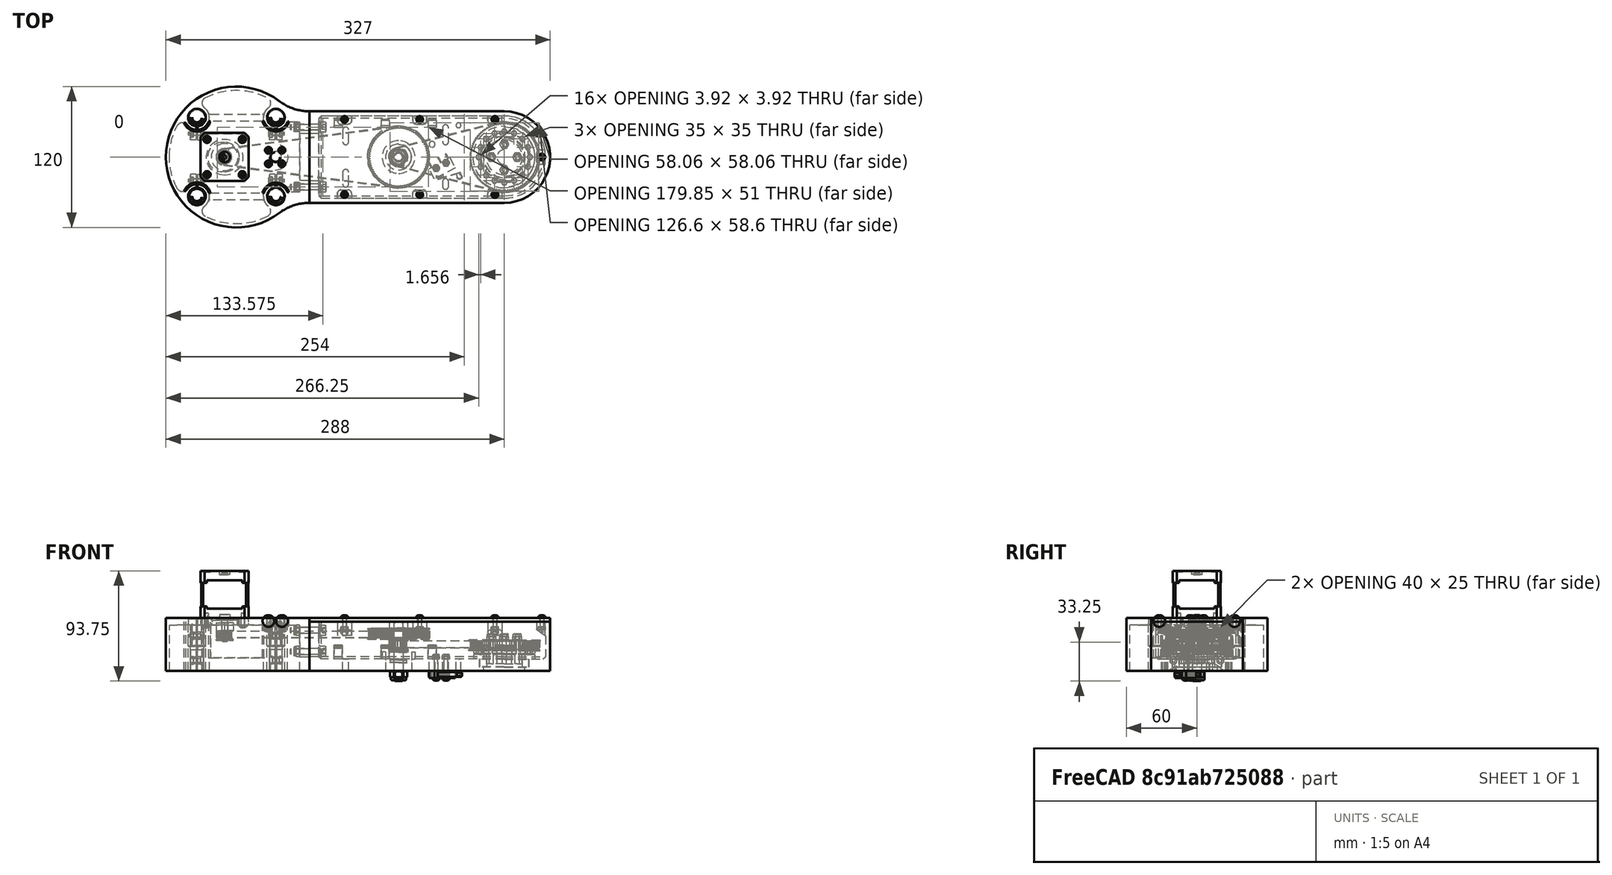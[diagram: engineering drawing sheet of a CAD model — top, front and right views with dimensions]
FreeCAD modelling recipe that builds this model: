
FCSTD DOCUMENT  (FreeCAD 0.19R)
Label: Arm1_a2p
License: All rights reserved
LicenseURL: http://en.wikipedia.org/wiki/All_rights_reserved
objects: Part::FeaturePython×76, App::FeaturePython×51, Spreadsheet::Sheet×2
note: 76 computed .brp shape members not serialized (recipe doc carries the construction recipe); baked Part::Feature solids carry a one-line shape summary decoded from their .brp

FEATURE [Part::FeaturePython] b_Arm1_modified_001_  label="Arm1_modified_001"  # a2plus imported part (geometry in sourceFile) (typed FeaturePython)
  a2p_Version = V0.1
  fixedPosition = true
  muxInfo = <blob: 26988 chars omitted>
  objectType = a2pPart
  sourceFile = ./Arm1_modified.FCStd
  subassemblyImport = false
  timeLastImport = 1.62074e+09
  updateColors = true
FEATURE [App::FeaturePython] circularEdge_001_mirror  label="circularEdge_001__Z-axis_mount_platform_LM8_001"  # a2plus constraint (typed FeaturePython)
  Object1 = b_Z_axis_mount_platform_LM8_001_
  Object2 = b_Arm1_modified_001_
  ParentTreeObject = -> b_Arm1_modified_001_
  SubElement1 = Edge12
  SubElement2 = Edge175
  Suppressed = false
  Type = circularEdge
  directionConstraint = 1
  lockRotation = true
  offset = 0
FEATURE [Part::FeaturePython] b_Ball_bearing_6081_001_  label="Ball_bearing_6081_001"  # a2plus imported part (geometry in sourceFile) (typed FeaturePython)
  Placement = pos=(-90,-3.743e-12,9) rot=(1,0,0;1.5708rad)
  a2p_Version = V0.1
  fixedPosition = false
  muxInfo = <blob: 2406 chars omitted>
  objectType = a2pPart
  sourceFile = ./Ball_bearing_608.step
  subassemblyImport = false
  timeLastImport = 1.62025e+09
  updateColors = true
FEATURE [App::FeaturePython] circularEdge_002  label="circularEdge_002__Arm1_modified_001"  # a2plus constraint (typed FeaturePython)
  Object1 = b_Ball_bearing_6081_001_
  Object2 = b_Arm1_modified_001_
  ParentTreeObject = -> b_Ball_bearing_6081_001_
  SubElement1 = Edge43
  SubElement2 = Edge634
  Suppressed = false
  Type = circularEdge
  directionConstraint = 1
  lockRotation = false
  offset = 0
FEATURE [App::FeaturePython] circularEdge_002_mirror  label="circularEdge_002__Ball_bearing_6081_001"  # a2plus constraint (typed FeaturePython)
  Object1 = b_Ball_bearing_6081_001_
  Object2 = b_Arm1_modified_001_
  ParentTreeObject = -> b_Arm1_modified_001_
  SubElement1 = Edge43
  SubElement2 = Edge634
  Suppressed = false
  Type = circularEdge
  directionConstraint = 1
  lockRotation = false
  offset = 0
FEATURE [Part::FeaturePython] b_Ball_bearing_6081_001_001  label="Ball_bearing_6081_002"  # a2plus imported part (geometry in sourceFile) (typed FeaturePython)
  Placement = pos=(-90,-1.2387e-07,-8.87936e-09) rot=(1,0,0;1.5708rad)
  a2p_Version = V0.1
  fixedPosition = false
  muxInfo = <blob: 2406 chars omitted>
  objectType = a2pPart
  sourceFile = ./Ball_bearing_608.step
  subassemblyImport = false
  timeLastImport = 1.62025e+09
  updateColors = true
FEATURE [App::FeaturePython] circularEdge_003  label="circularEdge_003__Arm1_modified_001"  # a2plus constraint (typed FeaturePython)
  Object1 = b_Ball_bearing_6081_001_001
  Object2 = b_Arm1_modified_001_
  ParentTreeObject = -> b_Ball_bearing_6081_001_001
  SubElement1 = Edge13
  SubElement2 = Edge459
  Suppressed = false
  Type = circularEdge
  directionConstraint = 1
  lockRotation = false
  offset = 0
FEATURE [App::FeaturePython] circularEdge_003_mirror  label="circularEdge_003__Ball_bearing_6081_002"  # a2plus constraint (typed FeaturePython)
  Object1 = b_Ball_bearing_6081_001_001
  Object2 = b_Arm1_modified_001_
  ParentTreeObject = -> b_Arm1_modified_001_
  SubElement1 = Edge13
  SubElement2 = Edge459
  Suppressed = false
  Type = circularEdge
  directionConstraint = 1
  lockRotation = false
  offset = 0
FEATURE [Part::FeaturePython] b_Ball_bearing_68061_001_  label="Ball_bearing_68061_001"  # a2plus imported part (geometry in sourceFile) (typed FeaturePython)
  Placement = pos=(0,1e-15,3) rot=(1,0,0;1.5708rad)
  a2p_Version = V0.1
  fixedPosition = false
  muxInfo = <blob: 2407 chars omitted>
  objectType = a2pPart
  sourceFile = ./Ball_bearing_6806.step
  subassemblyImport = false
  timeLastImport = 1.62074e+09
  updateColors = true
FEATURE [App::FeaturePython] circularEdge_004  label="circularEdge_004__Arm1_modified_001"  # a2plus constraint (typed FeaturePython)
  Object1 = b_Ball_bearing_68061_001_
  Object2 = b_Arm1_modified_001_
  ParentTreeObject = -> b_Ball_bearing_68061_001_
  SubElement1 = Edge21
  SubElement2 = Edge539
  Suppressed = false
  Type = circularEdge
  directionConstraint = 1
  lockRotation = false
  offset = 0
FEATURE [App::FeaturePython] circularEdge_004_mirror  label="circularEdge_004__Ball_bearing_68061_001"  # a2plus constraint (typed FeaturePython)
  Object1 = b_Ball_bearing_68061_001_
  Object2 = b_Arm1_modified_001_
  ParentTreeObject = -> b_Arm1_modified_001_
  SubElement1 = Edge21
  SubElement2 = Edge539
  Suppressed = false
  Type = circularEdge
  directionConstraint = 1
  lockRotation = false
  offset = 0
FEATURE [Part::FeaturePython] b_Thrust_bearing_511071_001_  label="Thrust_bearing_511071_001"  # a2plus imported part (geometry in sourceFile) (typed FeaturePython)
  Placement = pos=(0,2e-15,10) rot=(1,0,0;1.5708rad)
  a2p_Version = V0.1
  fixedPosition = false
  muxInfo = <blob: 16793 chars omitted>
  objectType = a2pPart
  sourceFile = ./Thrust_bearing_51107.step
  subassemblyImport = false
  timeLastImport = 1.62025e+09
  updateColors = true
FEATURE [App::FeaturePython] circularEdge_005  label="circularEdge_005__Arm1_modified_001"  # a2plus constraint (typed FeaturePython)
  Object1 = b_Thrust_bearing_511071_001_
  Object2 = b_Arm1_modified_001_
  ParentTreeObject = -> b_Thrust_bearing_511071_001_
  SubElement1 = Edge18
  SubElement2 = Edge395
  Suppressed = false
  Type = circularEdge
  directionConstraint = 1
  lockRotation = false
  offset = 0
FEATURE [App::FeaturePython] circularEdge_005_mirror  label="circularEdge_005__Thrust_bearing_511071_001"  # a2plus constraint (typed FeaturePython)
  Object1 = b_Thrust_bearing_511071_001_
  Object2 = b_Arm1_modified_001_
  ParentTreeObject = -> b_Arm1_modified_001_
  SubElement1 = Edge18
  SubElement2 = Edge395
  Suppressed = false
  Type = circularEdge
  directionConstraint = 1
  lockRotation = false
  offset = 0
FEATURE [Part::FeaturePython] b_Pulley_GT2_92t_j21_001_  label="Pulley_GT2-92t_j21_001"  # a2plus imported part (geometry in sourceFile) (typed FeaturePython)
  Placement = pos=(0,8.12133e-08,18.2) rot=(1,0,0;1.5708rad)
  a2p_Version = V0.1
  fixedPosition = false
  muxInfo = <blob: 117975 chars omitted>
  objectType = a2pPart
  sourceFile = ./Pulley_GT2-92t_j2.step
  subassemblyImport = false
  timeLastImport = 1.62074e+09
  updateColors = true
FEATURE [App::FeaturePython] circularEdge_006  label="circularEdge_006__Thrust_bearing_511071_001"  # a2plus constraint (typed FeaturePython)
  Object1 = b_Pulley_GT2_92t_j21_001_
  Object2 = b_Thrust_bearing_511071_001_
  ParentTreeObject = -> b_Pulley_GT2_92t_j21_001_
  SubElement1 = Edge2523
  SubElement2 = Edge29
  Suppressed = false
  Type = circularEdge
  directionConstraint = 1
  lockRotation = false
  offset = 0
FEATURE [App::FeaturePython] circularEdge_006_mirror  label="circularEdge_006__Pulley_GT2-92t_j21_001"  # a2plus constraint (typed FeaturePython)
  Object1 = b_Pulley_GT2_92t_j21_001_
  Object2 = b_Thrust_bearing_511071_001_
  ParentTreeObject = -> b_Thrust_bearing_511071_001_
  SubElement1 = Edge2523
  SubElement2 = Edge29
  Suppressed = false
  Type = circularEdge
  directionConstraint = 1
  lockRotation = false
  offset = 0
FEATURE [Part::FeaturePython] Washer  label="M8-Washer"  # Fasteners workbench fastener (typed FeaturePython)
  Placement = pos=(-90,1.17671e-07,16) rot=(0,0,1;0rad)
  baseObject = -> b_Ball_bearing_6081_001_ [Edge39]
  diameter = 8
  invert = true
  matchOuter = false
  offset = 0
  type = 3
FEATURE [Part::FeaturePython] b_Pulley_GT2_23t_80t_arm11_001_  label="Pulley_GT2-23t_80t_arm11_001"  # a2plus imported part (geometry in sourceFile) (typed FeaturePython)
  Placement = pos=(-90,9.54168e-07,35.05) rot=(0.229954,-0.688157,0.688157;3.59364rad)
  a2p_Version = V0.1
  fixedPosition = false
  muxInfo = <blob: 130900 chars omitted>
  objectType = a2pPart
  sourceFile = ./Pulley_GT2-23t_80t_arm1.step
  subassemblyImport = false
  timeLastImport = 1.62074e+09
  updateColors = true
FEATURE [App::FeaturePython] circularEdge_007  label="circularEdge_007__Ball_bearing_6081_001"  # a2plus constraint (typed FeaturePython)
  Object1 = b_Pulley_GT2_23t_80t_arm11_001_
  Object2 = b_Ball_bearing_6081_001_
  ParentTreeObject = -> b_Pulley_GT2_23t_80t_arm11_001_
  SubElement1 = Edge2268
  SubElement2 = Edge13
  Suppressed = false
  Type = circularEdge
  directionConstraint = 1
  lockRotation = false
  offset = -1.45
FEATURE [App::FeaturePython] circularEdge_007_mirror  label="circularEdge_007__Pulley_GT2-23t_80t_arm11_001"  # a2plus constraint (typed FeaturePython)
  Object1 = b_Pulley_GT2_23t_80t_arm11_001_
  Object2 = b_Ball_bearing_6081_001_
  ParentTreeObject = -> b_Ball_bearing_6081_001_
  SubElement1 = Edge2268
  SubElement2 = Edge13
  Suppressed = false
  Type = circularEdge
  directionConstraint = 1
  lockRotation = false
  offset = -1.45
FEATURE [Part::FeaturePython] b_Belt_GT2_300mm_23_92_arm11_001_  label="Belt_GT2_300mm_23-92_arm11_001"  # a2plus imported part (geometry in sourceFile) (typed FeaturePython)
  Placement = pos=(-2.93982e-09,1.75969e-07,19.65) rot=(1,0,0;1.5708rad)
  a2p_Version = V0.1
  fixedPosition = false
  muxInfo = [VERTEXES] | V;Part__Feature;1; | V;Part__Feature;2; | V;Part__Feature;3; | V;Part__Feature;4; | V;Part__Feature;5; | V;Part__Feature;6; | V;Part__Feature;7; | V;Part__Feature;8; | V;Part__Feature;9; | V;Part__Feature;10; | V;Part__Feature;11; | V;Part__Feature;12; | V;Part__Feature;13; | V;Part__Feature;14; | V;Part__Feature;15; | V;Part__Feature;16; | V;Part__Feature;17; | V;Part__Feature;18; | V;Part__Feature;19; | V;Part__Feature;20; | V;Part__Feature;21; | V;Part__Feature;22; | V;Part__Feature;23; | V;Part__Feature;24; | [EDGES] | E;Part__Feature;1; | E;Part__Feature;2; | E;Part__Feature;3; | E;Part__Feature;4; | E;Part__Feature;2; | E;Part__Feature;5; | E;Part__Feature;4; | E;Part__Feature;6; | E;Part__Feature;7; | E;Part__Feature;8; | E;Part__Feature;9; | E;Part__Feature;6; | E;Part__Feature;8; | E;Part__Feature;10; | E;Part__Feature;11; | E;Part__Feature;12; | E;Part__Feature;6; | E;Part__Feature;13; | E;Part__Feature;14; | E;Part__Feature;15; | E;Part__Feature;16; | E;Part__Feature;4; | E;Part__Feature;17; | E;Part__Feature;18; | E;Part__Feature;8; | E;Part__Feature;19; | E;Part__Feature;20; | E;Part__Feature;21; | E;Part__Feature;2; | E;Part__Feature;22; | E;Part__Feature;23; | E;Part__Feature;24; | E;Part__Feature;25; | E;Part__Feature;26; | E;Part__Feature;27; | E;Part__Feature;28; | [FACES] | F;Part__Feature;1; | F;Part__Feature;1; | F;Part__Feature;2; | F;Part__Feature;2; | F;Part__Feature;3; | F;Part__Feature;4; | F;Part__Feature;5; | F;Part__Feature;6; | F;Part__Feature;2; | F;Part__Feature;7; | F;Part__Feature;8; | F;Part__Feature;9; | F;Part__Feature;1; | F;Part__Feature;10;
  objectType = a2pPart
  sourceFile = ./Belt_GT2_300mm_23-92_arm1.step
  subassemblyImport = false
  timeLastImport = 1.62074e+09
  updateColors = true
FEATURE [App::FeaturePython] circularEdge_001  label="circularEdge_001__Pulley_GT2-23t_80t_arm11_001"  # a2plus constraint (typed FeaturePython)
  Object1 = b_Belt_GT2_300mm_23_92_arm11_001_
  Object2 = b_Pulley_GT2_23t_80t_arm11_001_
  ParentTreeObject = -> b_Belt_GT2_300mm_23_92_arm11_001_
  SubElement1 = Edge15
  SubElement2 = Edge1
  Suppressed = false
  Type = circularEdge
  directionConstraint = 1
  lockRotation = false
  offset = 0
FEATURE [App::FeaturePython] circularEdge_001_mirror001  label="circularEdge_001__Belt_GT2_300mm_23-92_arm11_001"  # a2plus constraint (typed FeaturePython)
  Object1 = b_Belt_GT2_300mm_23_92_arm11_001_
  Object2 = b_Pulley_GT2_23t_80t_arm11_001_
  ParentTreeObject = -> b_Pulley_GT2_23t_80t_arm11_001_
  SubElement1 = Edge15
  SubElement2 = Edge1
  Suppressed = false
  Type = circularEdge
  directionConstraint = 1
  lockRotation = false
  offset = 0
FEATURE [App::FeaturePython] axisCoincident_001  label="axisCoincident_001__Pulley_GT2-92t_j21_001"  # a2plus constraint (typed FeaturePython)
  Object1 = b_Belt_GT2_300mm_23_92_arm11_001_
  Object2 = b_Pulley_GT2_92t_j21_001_
  ParentTreeObject = -> b_Belt_GT2_300mm_23_92_arm11_001_
  SubElement1 = Face3
  SubElement2 = Face12
  Suppressed = false
  Type = axial
  directionConstraint = 0
  lockRotation = false
FEATURE [App::FeaturePython] axisCoincident_001_mirror  label="axisCoincident_001__Belt_GT2_300mm_23-92_arm11_001"  # a2plus constraint (typed FeaturePython)
  Object1 = b_Belt_GT2_300mm_23_92_arm11_001_
  Object2 = b_Pulley_GT2_92t_j21_001_
  ParentTreeObject = -> b_Pulley_GT2_92t_j21_001_
  SubElement1 = Face3
  SubElement2 = Face12
  Suppressed = false
  Type = axial
  directionConstraint = 0
  lockRotation = false
FEATURE [Part::FeaturePython] b_Belt_GT2_400mm_20_80_arm11_001_  label="Belt_GT2_400mm_20-80_arm11_001"  # a2plus imported part (geometry in sourceFile) (typed FeaturePython)
  Placement = pos=(-90,5.96931e-07,28.05) rot=(1,0,0;1.5708rad)
  a2p_Version = V0.1
  fixedPosition = false
  muxInfo = [VERTEXES] | V;Part__Feature;1; | V;Part__Feature;2; | V;Part__Feature;3; | V;Part__Feature;4; | V;Part__Feature;5; | V;Part__Feature;6; | V;Part__Feature;7; | V;Part__Feature;8; | V;Part__Feature;9; | V;Part__Feature;10; | V;Part__Feature;11; | V;Part__Feature;12; | V;Part__Feature;13; | V;Part__Feature;14; | V;Part__Feature;15; | V;Part__Feature;16; | V;Part__Feature;17; | V;Part__Feature;18; | V;Part__Feature;19; | V;Part__Feature;20; | V;Part__Feature;21; | V;Part__Feature;22; | V;Part__Feature;23; | V;Part__Feature;24; | [EDGES] | E;Part__Feature;1; | E;Part__Feature;2; | E;Part__Feature;3; | E;Part__Feature;4; | E;Part__Feature;2; | E;Part__Feature;5; | E;Part__Feature;4; | E;Part__Feature;6; | E;Part__Feature;7; | E;Part__Feature;8; | E;Part__Feature;9; | E;Part__Feature;6; | E;Part__Feature;8; | E;Part__Feature;10; | E;Part__Feature;11; | E;Part__Feature;12; | E;Part__Feature;6; | E;Part__Feature;13; | E;Part__Feature;14; | E;Part__Feature;15; | E;Part__Feature;16; | E;Part__Feature;4; | E;Part__Feature;17; | E;Part__Feature;18; | E;Part__Feature;8; | E;Part__Feature;19; | E;Part__Feature;20; | E;Part__Feature;21; | E;Part__Feature;2; | E;Part__Feature;22; | E;Part__Feature;23; | E;Part__Feature;24; | E;Part__Feature;25; | E;Part__Feature;26; | E;Part__Feature;27; | E;Part__Feature;28; | [FACES] | F;Part__Feature;1; | F;Part__Feature;1; | F;Part__Feature;2; | F;Part__Feature;2; | F;Part__Feature;3; | F;Part__Feature;4; | F;Part__Feature;5; | F;Part__Feature;6; | F;Part__Feature;2; | F;Part__Feature;7; | F;Part__Feature;8; | F;Part__Feature;9; | F;Part__Feature;1; | F;Part__Feature;10;
  objectType = a2pPart
  sourceFile = ./Belt_GT2_400mm_20-80_arm1.step
  subassemblyImport = false
  timeLastImport = 1.62074e+09
  updateColors = true
FEATURE [App::FeaturePython] circularEdge_008  label="circularEdge_008__Pulley_GT2-23t_80t_arm11_001"  # a2plus constraint (typed FeaturePython)
  Object1 = b_Belt_GT2_400mm_20_80_arm11_001_
  Object2 = b_Pulley_GT2_23t_80t_arm11_001_
  ParentTreeObject = -> b_Belt_GT2_400mm_20_80_arm11_001_
  SubElement1 = Edge5
  SubElement2 = Edge107
  Suppressed = false
  Type = circularEdge
  directionConstraint = 0
  lockRotation = false
  offset = 0
FEATURE [App::FeaturePython] circularEdge_008_mirror  label="circularEdge_008__Belt_GT2_400mm_20-80_arm11_001"  # a2plus constraint (typed FeaturePython)
  Object1 = b_Belt_GT2_400mm_20_80_arm11_001_
  Object2 = b_Pulley_GT2_23t_80t_arm11_001_
  ParentTreeObject = -> b_Pulley_GT2_23t_80t_arm11_001_
  SubElement1 = Edge5
  SubElement2 = Edge107
  Suppressed = false
  Type = circularEdge
  directionConstraint = 0
  lockRotation = false
  offset = 0
FEATURE [Part::FeaturePython] b_Z_axis_mount_platform_LM8_001_  label="Z-axis_mount_platform_LM8_001"  # a2plus imported part (geometry in sourceFile) (typed FeaturePython)
  Placement = pos=(-228,1.51055e-06,45) rot=(0.57735,-0.57735,0.57735;4.18879rad)
  a2p_Version = V0.1
  fixedPosition = false
  muxInfo = <blob: 41911 chars omitted>
  objectType = a2pPart
  sourceFile = ./Z-axis_mount_platform_LM8.FCStd
  subassemblyImport = false
  timeLastImport = 1.62026e+09
  updateColors = true
FEATURE [App::FeaturePython] circularEdge_009  label="circularEdge_009__Arm1_modified_001"  # a2plus constraint (typed FeaturePython)
  Object1 = b_Z_axis_mount_platform_LM8_001_
  Object2 = b_Arm1_modified_001_
  ParentTreeObject = -> b_Z_axis_mount_platform_LM8_001_
  SubElement1 = Edge9
  SubElement2 = Edge170
  Suppressed = false
  Type = circularEdge
  directionConstraint = 1
  lockRotation = false
  offset = 0
FEATURE [App::FeaturePython] circularEdge_009_mirror  label="circularEdge_009__Z-axis_mount_platform_LM8_001"  # a2plus constraint (typed FeaturePython)
  Object1 = b_Z_axis_mount_platform_LM8_001_
  Object2 = b_Arm1_modified_001_
  ParentTreeObject = -> b_Arm1_modified_001_
  SubElement1 = Edge9
  SubElement2 = Edge170
  Suppressed = false
  Type = circularEdge
  directionConstraint = 1
  lockRotation = false
  offset = 0
FEATURE [App::FeaturePython] axisCoincident_002  label="axisCoincident_002__Z-axis_mount_platform_LM8_001"  # a2plus constraint (typed FeaturePython)
  Object1 = b_Arm1_modified_001_
  Object2 = b_Z_axis_mount_platform_LM8_001_
  ParentTreeObject = -> b_Arm1_modified_001_
  SubElement1 = Face46
  SubElement2 = Face6
  Suppressed = false
  Type = axial
  directionConstraint = 1
  lockRotation = false
FEATURE [App::FeaturePython] axisCoincident_002_mirror  label="axisCoincident_002__Arm1_modified_001"  # a2plus constraint (typed FeaturePython)
  Object1 = b_Arm1_modified_001_
  Object2 = b_Z_axis_mount_platform_LM8_001_
  ParentTreeObject = -> b_Z_axis_mount_platform_LM8_001_
  SubElement1 = Face46
  SubElement2 = Face6
  Suppressed = false
  Type = axial
  directionConstraint = 1
  lockRotation = false
FEATURE [Part::FeaturePython] b_Stepper_NEMA_17____20mm_shaft1_001_  label="Stepper NEMA 17 -  20mm shaft1_001"  # a2plus imported part (geometry in sourceFile) (typed FeaturePython)
  Placement = pos=(-275.229,-8.46137,106.026) rot=(0.707107,0.707107,0;3.14159rad)
  a2p_Version = V0.1
  fixedPosition = false
  muxInfo = <blob: 18848 chars omitted>
  objectType = a2pPart
  sourceFile = ./Stepper NEMA 17 -  20mm shaft.step
  subassemblyImport = false
  timeLastImport = 1598802185
  updateColors = true
FEATURE [App::FeaturePython] circularEdge_010  label="circularEdge_010__Z-axis_mount_platform_LM8_001"  # a2plus constraint (typed FeaturePython)
  Object1 = b_Stepper_NEMA_17____20mm_shaft1_001_
  Object2 = b_Z_axis_mount_platform_LM8_001_
  ParentTreeObject = -> b_Stepper_NEMA_17____20mm_shaft1_001_
  SubElement1 = Edge53
  SubElement2 = Edge78
  Suppressed = false
  Type = circularEdge
  directionConstraint = 1
  lockRotation = false
  offset = 0
FEATURE [App::FeaturePython] circularEdge_010_mirror  label="circularEdge_010__Stepper NEMA 17 -  20mm shaft1_001"  # a2plus constraint (typed FeaturePython)
  Object1 = b_Stepper_NEMA_17____20mm_shaft1_001_
  Object2 = b_Z_axis_mount_platform_LM8_001_
  ParentTreeObject = -> b_Z_axis_mount_platform_LM8_001_
  SubElement1 = Edge53
  SubElement2 = Edge78
  Suppressed = false
  Type = circularEdge
  directionConstraint = 1
  lockRotation = false
  offset = 0
FEATURE [App::FeaturePython] axisCoincident_003  label="axisCoincident_003__Z-axis_mount_platform_LM8_001"  # a2plus constraint (typed FeaturePython)
  Object1 = b_Stepper_NEMA_17____20mm_shaft1_001_
  Object2 = b_Z_axis_mount_platform_LM8_001_
  ParentTreeObject = -> b_Stepper_NEMA_17____20mm_shaft1_001_
  SubElement1 = Face8
  SubElement2 = Face68
  Suppressed = false
  Type = axial
  directionConstraint = 1
  lockRotation = false
FEATURE [App::FeaturePython] axisCoincident_003_mirror  label="axisCoincident_003__Stepper NEMA 17 -  20mm shaft1_001"  # a2plus constraint (typed FeaturePython)
  Object1 = b_Stepper_NEMA_17____20mm_shaft1_001_
  Object2 = b_Z_axis_mount_platform_LM8_001_
  ParentTreeObject = -> b_Z_axis_mount_platform_LM8_001_
  SubElement1 = Face8
  SubElement2 = Face68
  Suppressed = false
  Type = axial
  directionConstraint = 1
  lockRotation = false
FEATURE [Part::FeaturePython] b_Pulley_GT2_20t1_001_  label="Pulley_GT2-20t1_001"  # a2plus imported part (geometry in sourceFile) (typed FeaturePython)
  Placement = pos=(-168.743,-32.2954,53.3499) rot=(1,0,0;1.5708rad)
  a2p_Version = V0.1
  fixedPosition = false
  muxInfo = <blob: 25437 chars omitted>
  objectType = a2pPart
  sourceFile = ./Pulley_GT2-20t.step
  subassemblyImport = false
  timeLastImport = 1.62073e+09
  updateColors = true
FEATURE [App::FeaturePython] axisCoincident_004  label="axisCoincident_004__Stepper NEMA 17 -  20mm shaft1_001"  # a2plus constraint (typed FeaturePython)
  Object1 = b_Pulley_GT2_20t1_001_
  Object2 = b_Stepper_NEMA_17____20mm_shaft1_001_
  ParentTreeObject = -> b_Pulley_GT2_20t1_001_
  SubElement1 = Face190
  SubElement2 = Face21
  Suppressed = false
  Type = axial
  directionConstraint = 1
  lockRotation = false
FEATURE [App::FeaturePython] axisCoincident_004_mirror  label="axisCoincident_004__Pulley_GT2-20t1_001"  # a2plus constraint (typed FeaturePython)
  Object1 = b_Pulley_GT2_20t1_001_
  Object2 = b_Stepper_NEMA_17____20mm_shaft1_001_
  ParentTreeObject = -> b_Stepper_NEMA_17____20mm_shaft1_001_
  SubElement1 = Face190
  SubElement2 = Face21
  Suppressed = false
  Type = axial
  directionConstraint = 1
  lockRotation = false
FEATURE [App::FeaturePython] circularEdge_011  label="circularEdge_011__Pulley_GT2-20t1_001"  # a2plus constraint (typed FeaturePython)
  Object1 = b_Belt_GT2_400mm_20_80_arm11_001_
  Object2 = b_Pulley_GT2_20t1_001_
  ParentTreeObject = -> b_Belt_GT2_400mm_20_80_arm11_001_
  SubElement1 = Edge20
  SubElement2 = Edge1
  Suppressed = false
  Type = circularEdge
  directionConstraint = 1
  lockRotation = false
  offset = 0
FEATURE [App::FeaturePython] circularEdge_011_mirror  label="circularEdge_011__Belt_GT2_400mm_20-80_arm11_001"  # a2plus constraint (typed FeaturePython)
  Object1 = b_Belt_GT2_400mm_20_80_arm11_001_
  Object2 = b_Pulley_GT2_20t1_001_
  ParentTreeObject = -> b_Pulley_GT2_20t1_001_
  SubElement1 = Edge20
  SubElement2 = Edge1
  Suppressed = false
  Type = circularEdge
  directionConstraint = 1
  lockRotation = false
  offset = 0
FEATURE [Part::FeaturePython] b_Nut_TR8_brass1_001_  label="Nut_TR8_brass1_001"  # a2plus imported part (geometry in sourceFile) (typed FeaturePython)
  Placement = pos=(-195,1.021e-06,37.5) rot=(1,0,0;1.5708rad)
  a2p_Version = V0.1
  fixedPosition = false
  muxInfo = <blob: 2191 chars omitted>
  objectType = a2pPart
  sourceFile = ./Nut_TR8_brass.step
  subassemblyImport = false
  timeLastImport = 1.62025e+09
  updateColors = true
FEATURE [App::FeaturePython] circularEdge_012  label="circularEdge_012__Z-axis_mount_platform_LM8_001"  # a2plus constraint (typed FeaturePython)
  Object1 = b_Nut_TR8_brass1_001_
  Object2 = b_Z_axis_mount_platform_LM8_001_
  ParentTreeObject = -> b_Nut_TR8_brass1_001_
  SubElement1 = Edge23
  SubElement2 = Edge323
  Suppressed = false
  Type = circularEdge
  directionConstraint = 0
  lockRotation = false
  offset = 0
FEATURE [App::FeaturePython] circularEdge_012_mirror  label="circularEdge_012__Nut_TR8_brass1_001"  # a2plus constraint (typed FeaturePython)
  Object1 = b_Nut_TR8_brass1_001_
  Object2 = b_Z_axis_mount_platform_LM8_001_
  ParentTreeObject = -> b_Z_axis_mount_platform_LM8_001_
  SubElement1 = Edge23
  SubElement2 = Edge323
  Suppressed = false
  Type = circularEdge
  directionConstraint = 0
  lockRotation = false
  offset = 0
FEATURE [App::FeaturePython] axisCoincident_005  label="axisCoincident_005__Z-axis_mount_platform_LM8_001"  # a2plus constraint (typed FeaturePython)
  Object1 = b_Nut_TR8_brass1_001_
  Object2 = b_Z_axis_mount_platform_LM8_001_
  ParentTreeObject = -> b_Nut_TR8_brass1_001_
  SubElement1 = Face2
  SubElement2 = Face86
  Suppressed = false
  Type = axial
  directionConstraint = 1
  lockRotation = false
FEATURE [App::FeaturePython] axisCoincident_005_mirror  label="axisCoincident_005__Nut_TR8_brass1_001"  # a2plus constraint (typed FeaturePython)
  Object1 = b_Nut_TR8_brass1_001_
  Object2 = b_Z_axis_mount_platform_LM8_001_
  ParentTreeObject = -> b_Z_axis_mount_platform_LM8_001_
  SubElement1 = Face2
  SubElement2 = Face86
  Suppressed = false
  Type = axial
  directionConstraint = 1
  lockRotation = false
FEATURE [Part::FeaturePython] b_Linear_bearing_lm8uu1_001_  label="Linear_bearing_lm8uu1_001"  # a2plus imported part (geometry in sourceFile) (typed FeaturePython)
  Placement = pos=(-194.412,-33.5876,45) rot=(0.547548,-0.591689,0.591689;4.14351rad)
  a2p_Version = V0.1
  fixedPosition = false
  muxInfo = <blob: 2927 chars omitted>
  objectType = a2pPart
  sourceFile = ./Linear_bearing_lm8uu.step
  subassemblyImport = false
  timeLastImport = 1.62075e+09
  updateColors = true
FEATURE [App::FeaturePython] circularEdge_013  label="circularEdge_013__Z-axis_mount_platform_LM8_001"  # a2plus constraint (typed FeaturePython)
  Object1 = b_Linear_bearing_lm8uu1_001_
  Object2 = b_Z_axis_mount_platform_LM8_001_
  ParentTreeObject = -> b_Linear_bearing_lm8uu1_001_
  SubElement1 = Edge55
  SubElement2 = Edge125
  Suppressed = false
  Type = circularEdge
  directionConstraint = 0
  lockRotation = false
  offset = 0
FEATURE [App::FeaturePython] circularEdge_013_mirror  label="circularEdge_013__Linear_bearing_lm8uu1_001"  # a2plus constraint (typed FeaturePython)
  Object1 = b_Linear_bearing_lm8uu1_001_
  Object2 = b_Z_axis_mount_platform_LM8_001_
  ParentTreeObject = -> b_Z_axis_mount_platform_LM8_001_
  SubElement1 = Edge55
  SubElement2 = Edge125
  Suppressed = false
  Type = circularEdge
  directionConstraint = 0
  lockRotation = false
  offset = 0
FEATURE [Part::FeaturePython] b_Linear_bearing_lm8uu1_001_001  label="Linear_bearing_lm8uu1_002"  # a2plus imported part (geometry in sourceFile) (typed FeaturePython)
  Placement = pos=(-194.412,33.5876,45) rot=(0.547548,-0.591689,0.591689;4.14351rad)
  a2p_Version = V0.1
  fixedPosition = false
  muxInfo = <blob: 2927 chars omitted>
  objectType = a2pPart
  sourceFile = ./Linear_bearing_lm8uu.step
  subassemblyImport = false
  timeLastImport = 1.62075e+09
  updateColors = true
FEATURE [App::FeaturePython] circularEdge_014  label="circularEdge_014__Z-axis_mount_platform_LM8_001"  # a2plus constraint (typed FeaturePython)
  Object1 = b_Linear_bearing_lm8uu1_001_001
  Object2 = b_Z_axis_mount_platform_LM8_001_
  ParentTreeObject = -> b_Linear_bearing_lm8uu1_001_001
  SubElement1 = Edge9
  SubElement2 = Edge85
  Suppressed = false
  Type = circularEdge
  directionConstraint = 1
  lockRotation = false
  offset = 0
FEATURE [App::FeaturePython] circularEdge_014_mirror  label="circularEdge_014__Linear_bearing_lm8uu1_002"  # a2plus constraint (typed FeaturePython)
  Object1 = b_Linear_bearing_lm8uu1_001_001
  Object2 = b_Z_axis_mount_platform_LM8_001_
  ParentTreeObject = -> b_Z_axis_mount_platform_LM8_001_
  SubElement1 = Edge9
  SubElement2 = Edge85
  Suppressed = false
  Type = circularEdge
  directionConstraint = 1
  lockRotation = false
  offset = 0
FEATURE [Part::FeaturePython] b_Linear_bearing_lm8uu1_001_002  label="Linear_bearing_lm8uu1_003"  # a2plus imported part (geometry in sourceFile) (typed FeaturePython)
  Placement = pos=(-261.588,-33.5876,45) rot=(0.547548,-0.591689,0.591689;4.14351rad)
  a2p_Version = V0.1
  fixedPosition = false
  muxInfo = <blob: 2927 chars omitted>
  objectType = a2pPart
  sourceFile = ./Linear_bearing_lm8uu.step
  subassemblyImport = false
  timeLastImport = 1.62075e+09
  updateColors = true
FEATURE [App::FeaturePython] circularEdge_015  label="circularEdge_015__Z-axis_mount_platform_LM8_001"  # a2plus constraint (typed FeaturePython)
  Object1 = b_Linear_bearing_lm8uu1_001_002
  Object2 = b_Z_axis_mount_platform_LM8_001_
  ParentTreeObject = -> b_Linear_bearing_lm8uu1_001_002
  SubElement1 = Edge56
  SubElement2 = Edge110
  Suppressed = false
  Type = circularEdge
  directionConstraint = 1
  lockRotation = false
  offset = 0
FEATURE [App::FeaturePython] circularEdge_015_mirror  label="circularEdge_015__Linear_bearing_lm8uu1_003"  # a2plus constraint (typed FeaturePython)
  Object1 = b_Linear_bearing_lm8uu1_001_002
  Object2 = b_Z_axis_mount_platform_LM8_001_
  ParentTreeObject = -> b_Z_axis_mount_platform_LM8_001_
  SubElement1 = Edge56
  SubElement2 = Edge110
  Suppressed = false
  Type = circularEdge
  directionConstraint = 1
  lockRotation = false
  offset = 0
FEATURE [Part::FeaturePython] b_Linear_bearing_lm8uu1_001_003  label="Linear_bearing_lm8uu1_004"  # a2plus imported part (geometry in sourceFile) (typed FeaturePython)
  Placement = pos=(-261.588,33.5876,45) rot=(0.547548,-0.591689,0.591689;4.14351rad)
  a2p_Version = V0.1
  fixedPosition = false
  muxInfo = <blob: 2927 chars omitted>
  objectType = a2pPart
  sourceFile = ./Linear_bearing_lm8uu.step
  subassemblyImport = false
  timeLastImport = 1.62075e+09
  updateColors = true
FEATURE [App::FeaturePython] circularEdge_016  label="circularEdge_016__Z-axis_mount_platform_LM8_001"  # a2plus constraint (typed FeaturePython)
  Object1 = b_Linear_bearing_lm8uu1_001_003
  Object2 = b_Z_axis_mount_platform_LM8_001_
  ParentTreeObject = -> b_Linear_bearing_lm8uu1_001_003
  SubElement1 = Edge56
  SubElement2 = Edge68
  Suppressed = false
  Type = circularEdge
  directionConstraint = 1
  lockRotation = false
  offset = 0
FEATURE [App::FeaturePython] circularEdge_016_mirror  label="circularEdge_016__Linear_bearing_lm8uu1_004"  # a2plus constraint (typed FeaturePython)
  Object1 = b_Linear_bearing_lm8uu1_001_003
  Object2 = b_Z_axis_mount_platform_LM8_001_
  ParentTreeObject = -> b_Z_axis_mount_platform_LM8_001_
  SubElement1 = Edge56
  SubElement2 = Edge68
  Suppressed = false
  Type = circularEdge
  directionConstraint = 1
  lockRotation = false
  offset = 0
FEATURE [Part::FeaturePython] b_Arm1_cover_modified_001_  label="Arm1_cover_modified_001"  # a2plus imported part (geometry in sourceFile) (typed FeaturePython)
  Placement = pos=(1e-15,-3.31558e-08,42) rot=(0,0,1;3.14159rad)
  a2p_Version = V0.1
  fixedPosition = false
  muxInfo = [VERTEXES] | V;Pad;1;22; | V;Pad;2;22; | V;Pad;3;22; | V;Pad;4;22; | V;Pad;5;22; | V;Pad;6;22; | V;Pad;7;22; | V;Pad;8;22; | V;Pad;9;22; | V;Pad;10;22; | V;Pad;11;22; | V;Pad;12;22; | V;Pad;13;22; | V;Pad;14;22; | V;Pad;15;22; | V;Pad;16;22; | V;Pad;17;22; | V;Pad;18;22; | V;Pad;19;22; | V;Pad;20;22; | V;Pad;21;22; | V;Pad;22;22; | [EDGES] | E;Pad;1;33; | E;Pad;2;33; | E;Pad;3;33; | E;Pad;4;33; | E;Pad;5;33; | E;Pad;6;33; | E;Pad;7;33; | E;Pad;8;33; | E;Pad;9;33; | E;Pad;10;33; | E;Pad;11;33; | E;Pad;12;33; | E;Pad;13;33; | E;Pad;14;33; | E;Pad;15;33; | E;Pad;16;33; | E;Pad;17;33; | E;Pad;18;33; | E;Pad;19;33; | E;Pad;20;33; | E;Pad;21;33; | E;Pad;22;33; | E;Pad;23;33; | E;Pad;24;33; | E;Pad;25;33; | E;Pad;26;33; | E;Pad;27;33; | E;Pad;28;33; | E;Pad;29;33; | E;Pad;30;33; | E;Pad;31;33; | E;Pad;32;33; | E;Pad;33;33; | [FACES] | F;Pad;1;13; | F;Pad;2;13; | F;Pad;3;13; | F;Pad;4;13; | F;Pad;5;13; | F;Pad;6;13; | F;Pad;7;13; | F;Pad;8;13; | F;Pad;9;13; | F;Pad;10;13; | F;Pad;11;13; | F;Pad;12;13; | F;Pad;13;13;
  objectType = a2pPart
  sourceFile = ./Arm1_cover_modified.FCStd
  subassemblyImport = false
  timeLastImport = 1.62075e+09
  updateColors = true
FEATURE [App::FeaturePython] circularEdge_017  label="circularEdge_017__Arm1_modified_001"  # a2plus constraint (typed FeaturePython)
  Object1 = b_Arm1_cover_modified_001_
  Object2 = b_Arm1_modified_001_
  ParentTreeObject = -> b_Arm1_cover_modified_001_
  SubElement1 = Edge3
  SubElement2 = Edge29
  Suppressed = false
  Type = circularEdge
  directionConstraint = 0
  lockRotation = false
  offset = 0
FEATURE [App::FeaturePython] circularEdge_017_mirror  label="circularEdge_017__Arm1_cover_modified_001"  # a2plus constraint (typed FeaturePython)
  Object1 = b_Arm1_cover_modified_001_
  Object2 = b_Arm1_modified_001_
  ParentTreeObject = -> b_Arm1_modified_001_
  SubElement1 = Edge3
  SubElement2 = Edge29
  Suppressed = false
  Type = circularEdge
  directionConstraint = 0
  lockRotation = false
  offset = 0
FEATURE [App::FeaturePython] planesParallel_001  label="planesParallel_001__Z-axis_mount_platform_LM8_001"  # a2plus constraint (typed FeaturePython)
  Object1 = b_Arm1_cover_modified_001_
  Object2 = b_Z_axis_mount_platform_LM8_001_
  ParentTreeObject = -> b_Arm1_cover_modified_001_
  SubElement1 = Face3
  SubElement2 = Face3
  Suppressed = false
  Type = planesParallel
  directionConstraint = 0
FEATURE [App::FeaturePython] planesParallel_001_mirror  label="planesParallel_001__Arm1_cover_modified_001"  # a2plus constraint (typed FeaturePython)
  Object1 = b_Arm1_cover_modified_001_
  Object2 = b_Z_axis_mount_platform_LM8_001_
  ParentTreeObject = -> b_Z_axis_mount_platform_LM8_001_
  SubElement1 = Face3
  SubElement2 = Face3
  Suppressed = false
  Type = planesParallel
  directionConstraint = 0
FEATURE [Part::FeaturePython] b_Switch_endstop1_001_  label="Switch_endstop1_001"  # a2plus imported part (geometry in sourceFile) (typed FeaturePython)
  Placement = pos=(-52.8531,-9.55473,2.09827e-07) rot=(0.970296,0.241922,0;3.14159rad)
  a2p_Version = V0.1
  fixedPosition = false
  muxInfo = <blob: 6853 chars omitted>
  objectType = a2pPart
  sourceFile = ./Switch_endstop.step
  subassemblyImport = false
  timeLastImport = 1.62073e+09
  updateColors = true
FEATURE [App::FeaturePython] circularEdge_018  label="circularEdge_018__Arm1_modified_001"  # a2plus constraint (typed FeaturePython)
  Object1 = b_Switch_endstop1_001_
  Object2 = b_Arm1_modified_001_
  ParentTreeObject = -> b_Switch_endstop1_001_
  SubElement1 = Edge39
  SubElement2 = Edge324
  Suppressed = false
  Type = circularEdge
  directionConstraint = 1
  lockRotation = false
  offset = 0
FEATURE [App::FeaturePython] circularEdge_018_mirror  label="circularEdge_018__Switch_endstop1_001"  # a2plus constraint (typed FeaturePython)
  Object1 = b_Switch_endstop1_001_
  Object2 = b_Arm1_modified_001_
  ParentTreeObject = -> b_Arm1_modified_001_
  SubElement1 = Edge39
  SubElement2 = Edge324
  Suppressed = false
  Type = circularEdge
  directionConstraint = 1
  lockRotation = false
  offset = 0
FEATURE [App::FeaturePython] axisCoincident_006  label="axisCoincident_006__Arm1_modified_001"  # a2plus constraint (typed FeaturePython)
  Object1 = b_Switch_endstop1_001_
  Object2 = b_Arm1_modified_001_
  ParentTreeObject = -> b_Switch_endstop1_001_
  SubElement1 = Face10
  SubElement2 = Face126
  Suppressed = false
  Type = axial
  directionConstraint = 1
  lockRotation = false
FEATURE [App::FeaturePython] axisCoincident_006_mirror  label="axisCoincident_006__Switch_endstop1_001"  # a2plus constraint (typed FeaturePython)
  Object1 = b_Switch_endstop1_001_
  Object2 = b_Arm1_modified_001_
  ParentTreeObject = -> b_Arm1_modified_001_
  SubElement1 = Face10
  SubElement2 = Face126
  Suppressed = false
  Type = axial
  directionConstraint = 1
  lockRotation = false
FEATURE [Part::FeaturePython] Screw  label="M3x10-Screw"  # Fasteners workbench fastener (typed FeaturePython)
  Placement = pos=(-253.5,-15.5,39) rot=(1,0,0;3.14159rad)
  baseObject = -> b_Z_axis_mount_platform_LM8_001_ [Edge243]
  diameter = 4
  invert = true
  length = 4
  lengthCustom = 10
  matchOuter = false
  offset = 0
  thread = false
  type = 34
FEATURE [Part::FeaturePython] Screw001  label="M3x10-Screw001"  # Fasteners workbench fastener (typed FeaturePython)
  Placement = pos=(-253.5,15.5,39) rot=(1,0,0;3.14159rad)
  baseObject = -> b_Z_axis_mount_platform_LM8_001_ [Edge222]
  diameter = 4
  invert = true
  length = 4
  lengthCustom = 10
  matchOuter = false
  offset = 0
  thread = false
  type = 34
FEATURE [Part::FeaturePython] Screw002  label="M3x10-Screw002"  # Fasteners workbench fastener (typed FeaturePython)
  Placement = pos=(-222.5,15.5,39) rot=(1,0,0;3.14159rad)
  baseObject = -> b_Z_axis_mount_platform_LM8_001_ [Edge217]
  diameter = 4
  invert = true
  length = 4
  lengthCustom = 10
  matchOuter = false
  offset = 0
  thread = false
  type = 34
FEATURE [Part::FeaturePython] Screw003  label="M3x10-Screw003"  # Fasteners workbench fastener (typed FeaturePython)
  Placement = pos=(-222.5,-15.5,39) rot=(1,0,0;3.14159rad)
  baseObject = -> b_Z_axis_mount_platform_LM8_001_ [Edge238]
  diameter = 4
  invert = true
  length = 4
  lengthCustom = 10
  matchOuter = false
  offset = 0
  thread = false
  type = 34
FEATURE [Part::FeaturePython] Screw004  label="M3x20-Screw"  # Fasteners workbench fastener (typed FeaturePython)
  Placement = pos=(-58,-9.45998,-6) rot=(0.882948,0.469471,0;3.14159rad)
  baseObject = -> b_Switch_endstop1_001_ [Edge36]
  diameter = 4
  invert = false
  length = 8
  lengthCustom = 20
  matchOuter = false
  offset = 0
  thread = false
  type = 34
FEATURE [Part::FeaturePython] Screw005  label="M3x20-Screw001"  # Fasteners workbench fastener (typed FeaturePython)
  Placement = pos=(-49.612,-5,-6) rot=(0.882948,0.469471,0;3.14159rad)
  baseObject = -> b_Switch_endstop1_001_ [Edge37]
  diameter = 4
  invert = false
  length = 8
  lengthCustom = 20
  matchOuter = false
  offset = 0
  thread = false
  type = 34
FEATURE [Part::FeaturePython] Nut  label="M8-Nut"  # Fasteners workbench fastener (typed FeaturePython)
  Placement = pos=(-90,-1.2387e-07,-8.87936e-09) rot=(1,0,0;3.14159rad)
  baseObject = -> b_Ball_bearing_6081_001_001 [Edge2]
  diameter = 6
  invert = true
  matchOuter = false
  offset = 0
  thread = false
  type = 5
FEATURE [Part::FeaturePython] Nut001  label="M3-Nut"  # Fasteners workbench fastener (typed FeaturePython)
  Placement = pos=(-200.75,5.75,37.5) rot=(0.998129,0.061139,0;3.14159rad)
  baseObject = -> b_Nut_TR8_brass1_001_ [Edge36]
  diameter = 1
  invert = false
  matchOuter = false
  offset = 0
  thread = false
  type = 5
FEATURE [Part::FeaturePython] Nut002  label="M3-Nut001"  # Fasteners workbench fastener (typed FeaturePython)
  Placement = pos=(-189.25,5.75,37.5) rot=(0.998129,0.061139,0;3.14159rad)
  baseObject = -> b_Nut_TR8_brass1_001_ [Edge12]
  diameter = 1
  invert = false
  matchOuter = false
  offset = 0
  thread = false
  type = 5
FEATURE [Part::FeaturePython] Nut003  label="M3-Nut002"  # Fasteners workbench fastener (typed FeaturePython)
  Placement = pos=(-189.25,-5.75,37.5) rot=(0.998129,0.061139,0;3.14159rad)
  baseObject = -> b_Nut_TR8_brass1_001_ [Edge34]
  diameter = 1
  invert = false
  matchOuter = false
  offset = 0
  thread = false
  type = 5
FEATURE [Part::FeaturePython] Nut004  label="M3-Nut003"  # Fasteners workbench fastener (typed FeaturePython)
  Placement = pos=(-200.75,-5.75,37.5) rot=(0.998129,0.061139,0;3.14159rad)
  baseObject = -> b_Nut_TR8_brass1_001_ [Edge4]
  diameter = 1
  invert = false
  matchOuter = false
  offset = 0
  thread = false
  type = 5
FEATURE [Part::FeaturePython] Screw006  label="M8x45-Screw"  # Fasteners workbench fastener (typed FeaturePython)
  Placement = pos=(-90,1.01553e-06,36.25) rot=(-0.289742,-0.957105,0;0rad)
  baseObject = -> b_Pulley_GT2_23t_80t_arm11_001_ [Edge114]
  diameter = 9
  invert = true
  length = 6
  lengthCustom = 45
  matchOuter = false
  offset = 0
  thread = false
  type = 28
FEATURE [Part::FeaturePython] Nut005  label="M4-Nut"  # Fasteners workbench fastener (typed FeaturePython)
  Placement = pos=(3e-15,11,26.4) rot=(0,0,1;0rad)
  baseObject = -> b_Pulley_GT2_92t_j21_001_ [Edge10]
  diameter = 2
  invert = false
  matchOuter = false
  offset = 0
  thread = false
  type = 5
FEATURE [Part::FeaturePython] Nut006  label="M4-Nut001"  # Fasteners workbench fastener (typed FeaturePython)
  Placement = pos=(11,3.65877e-07,26.4) rot=(0,0,1;0rad)
  baseObject = -> b_Pulley_GT2_92t_j21_001_ [Edge14]
  diameter = 2
  invert = false
  matchOuter = false
  offset = 0
  thread = false
  type = 5
FEATURE [Part::FeaturePython] Nut007  label="M4-Nut002"  # Fasteners workbench fastener (typed FeaturePython)
  Placement = pos=(-11,3.65877e-07,26.4) rot=(0,0,1;0rad)
  baseObject = -> b_Pulley_GT2_92t_j21_001_ [Edge2513]
  diameter = 2
  invert = false
  matchOuter = false
  offset = 0
  thread = false
  type = 5
FEATURE [Part::FeaturePython] Nut008  label="M4-Nut003"  # Fasteners workbench fastener (typed FeaturePython)
  Placement = pos=(1e-15,-11,26.4) rot=(0,0,1;0rad)
  baseObject = -> b_Pulley_GT2_92t_j21_001_ [Edge2]
  diameter = 2
  invert = false
  matchOuter = false
  offset = 0
  thread = false
  type = 5
FEATURE [Part::FeaturePython] Nut009  label="M3-Nut004"  # Fasteners workbench fastener (typed FeaturePython)
  Placement = pos=(-136,32,37.4) rot=(1,0,0;3.14159rad)
  baseObject = -> b_Arm1_modified_001_ [Edge51]
  diameter = 4
  invert = false
  matchOuter = false
  offset = 0
  thread = false
  type = 7
FEATURE [Part::FeaturePython] Nut010  label="M3-Nut005"  # Fasteners workbench fastener (typed FeaturePython)
  Placement = pos=(-72,32,37.4) rot=(1,0,0;3.14159rad)
  baseObject = -> b_Arm1_modified_001_ [Edge241]
  diameter = 4
  invert = false
  matchOuter = false
  offset = 0
  thread = false
  type = 7
FEATURE [Part::FeaturePython] Nut011  label="M3-Nut006"  # Fasteners workbench fastener (typed FeaturePython)
  Placement = pos=(-8,32,37.4) rot=(1,0,0;3.14159rad)
  baseObject = -> b_Arm1_modified_001_ [Edge280]
  diameter = 4
  invert = false
  matchOuter = false
  offset = 0
  thread = false
  type = 7
FEATURE [Part::FeaturePython] Nut012  label="M3-Nut007"  # Fasteners workbench fastener (typed FeaturePython)
  Placement = pos=(32,7e-15,37.4) rot=(1,0,0;3.14159rad)
  baseObject = -> b_Arm1_modified_001_ [Edge446]
  diameter = 4
  invert = false
  matchOuter = false
  offset = 0
  thread = false
  type = 7
FEATURE [Part::FeaturePython] Nut013  label="M3-Nut008"  # Fasteners workbench fastener (typed FeaturePython)
  Placement = pos=(-8,-32,37.4) rot=(1,0,0;3.14159rad)
  baseObject = -> b_Arm1_modified_001_ [Edge319]
  diameter = 4
  invert = false
  matchOuter = false
  offset = 0
  thread = false
  type = 7
FEATURE [Part::FeaturePython] Nut014  label="M3-Nut009"  # Fasteners workbench fastener (typed FeaturePython)
  Placement = pos=(-72,-32,37.4) rot=(1,0,0;3.14159rad)
  baseObject = -> b_Arm1_modified_001_ [Edge289]
  diameter = 4
  invert = false
  matchOuter = false
  offset = 0
  thread = false
  type = 7
FEATURE [Part::FeaturePython] Nut015  label="M3-Nut010"  # Fasteners workbench fastener (typed FeaturePython)
  Placement = pos=(-136,-32,37.4) rot=(1,0,0;3.14159rad)
  baseObject = -> b_Arm1_modified_001_ [Edge273]
  diameter = 4
  invert = false
  matchOuter = false
  offset = 0
  thread = false
  type = 7
FEATURE [Part::FeaturePython] Screw007  label="M3x12-Screw"  # Fasteners workbench fastener (typed FeaturePython)
  Placement = pos=(32,1.36117e-06,45) rot=(0,0,1;0rad)
  baseObject = -> b_Arm1_cover_modified_001_ [Edge33]
  diameter = 4
  invert = false
  length = 5
  lengthCustom = 12
  matchOuter = false
  offset = 0
  thread = false
  type = 34
FEATURE [Part::FeaturePython] Screw008  label="M3x12-Screw001"  # Fasteners workbench fastener (typed FeaturePython)
  Placement = pos=(-8,-32,45) rot=(0,0,1;0rad)
  baseObject = -> b_Arm1_cover_modified_001_ [Edge30]
  diameter = 4
  invert = false
  length = 5
  lengthCustom = 12
  matchOuter = false
  offset = 0
  thread = false
  type = 34
FEATURE [Part::FeaturePython] Screw009  label="M3x12-Screw002"  # Fasteners workbench fastener (typed FeaturePython)
  Placement = pos=(-8,32,45) rot=(0,0,1;0rad)
  baseObject = -> b_Arm1_cover_modified_001_ [Edge27]
  diameter = 4
  invert = false
  length = 5
  lengthCustom = 12
  matchOuter = false
  offset = 0
  thread = false
  type = 34
FEATURE [Part::FeaturePython] Screw010  label="M3x12-Screw003"  # Fasteners workbench fastener (typed FeaturePython)
  Placement = pos=(-72,32,45) rot=(0,0,1;0rad)
  baseObject = -> b_Arm1_cover_modified_001_ [Edge18]
  diameter = 4
  invert = false
  length = 5
  lengthCustom = 12
  matchOuter = false
  offset = 0
  thread = false
  type = 34
FEATURE [Part::FeaturePython] Screw011  label="M3x12-Screw004"  # Fasteners workbench fastener (typed FeaturePython)
  Placement = pos=(-72,-32,45) rot=(0,0,1;0rad)
  baseObject = -> b_Arm1_cover_modified_001_ [Edge24]
  diameter = 4
  invert = false
  length = 5
  lengthCustom = 12
  matchOuter = false
  offset = 0
  thread = false
  type = 34
FEATURE [Part::FeaturePython] Screw012  label="M3x12-Screw005"  # Fasteners workbench fastener (typed FeaturePython)
  Placement = pos=(-136,32,45) rot=(0,0,1;0rad)
  baseObject = -> b_Arm1_cover_modified_001_ [Edge15]
  diameter = 4
  invert = false
  length = 5
  lengthCustom = 12
  matchOuter = false
  offset = 0
  thread = false
  type = 34
FEATURE [Part::FeaturePython] Screw013  label="M3x12-Screw006"  # Fasteners workbench fastener (typed FeaturePython)
  Placement = pos=(-136,-32,45) rot=(0,0,1;0rad)
  baseObject = -> b_Arm1_cover_modified_001_ [Edge21]
  diameter = 4
  invert = false
  length = 5
  lengthCustom = 12
  matchOuter = false
  offset = 0
  thread = false
  type = 34
FEATURE [Part::FeaturePython] Screw014  label="M3x12-Screw007"  # Fasteners workbench fastener (typed FeaturePython)
  Placement = pos=(-189.25,-5.75,45) rot=(-1,0,0;0rad)
  baseObject = -> b_Z_axis_mount_platform_LM8_001_ [Edge119]
  diameter = 4
  invert = true
  length = 5
  lengthCustom = 12
  matchOuter = false
  offset = 0
  thread = false
  type = 34
FEATURE [Part::FeaturePython] Screw015  label="M3x12-Screw008"  # Fasteners workbench fastener (typed FeaturePython)
  Placement = pos=(-189.25,5.75,45) rot=(-1,0,0;0rad)
  baseObject = -> b_Z_axis_mount_platform_LM8_001_ [Edge97]
  diameter = 4
  invert = true
  length = 5
  lengthCustom = 12
  matchOuter = false
  offset = 0
  thread = false
  type = 34
FEATURE [Part::FeaturePython] Screw016  label="M3x12-Screw009"  # Fasteners workbench fastener (typed FeaturePython)
  Placement = pos=(-200.75,5.75,45) rot=(-1,0,0;0rad)
  baseObject = -> b_Z_axis_mount_platform_LM8_001_ [Edge93]
  diameter = 4
  invert = true
  length = 5
  lengthCustom = 12
  matchOuter = false
  offset = 0
  thread = false
  type = 34
FEATURE [Part::FeaturePython] Screw017  label="M3x12-Screw010"  # Fasteners workbench fastener (typed FeaturePython)
  Placement = pos=(-200.75,-5.75,45) rot=(-1,0,0;0rad)
  baseObject = -> b_Z_axis_mount_platform_LM8_001_ [Edge117]
  diameter = 4
  invert = true
  length = 5
  lengthCustom = 12
  matchOuter = false
  offset = 0
  thread = false
  type = 34
FEATURE [Part::FeaturePython] Nut016  label="M3-Nut011"  # Fasteners workbench fastener (typed FeaturePython)
  Placement = pos=(-58,-9.45998,10) rot=(0,0,1;0rad)
  baseObject = -> b_Arm1_modified_001_ [Edge368]
  diameter = 1
  invert = false
  matchOuter = false
  offset = 0
  thread = false
  type = 5
FEATURE [Part::FeaturePython] Nut017  label="M3-Nut012"  # Fasteners workbench fastener (typed FeaturePython)
  Placement = pos=(-49.612,-5,10) rot=(0,0,1;0rad)
  baseObject = -> b_Arm1_modified_001_ [Edge371]
  diameter = 1
  invert = false
  matchOuter = false
  offset = 0
  thread = false
  type = 5
FEATURE [Part::FeaturePython] Nut018  label="M3-Nut013"  # Fasteners workbench fastener (typed FeaturePython)
  Placement = pos=(-191.412,-20,29.9779) rot=(0,1,0;1.5708rad)
  baseObject = -> b_Z_axis_mount_platform_LM8_001_ [Edge804]
  diameter = 4
  invert = false
  matchOuter = false
  offset = 0
  thread = false
  type = 7
FEATURE [Part::FeaturePython] Nut019  label="M3-Nut014"  # Fasteners workbench fastener (typed FeaturePython)
  Placement = pos=(-191.412,20,29.9779) rot=(0,1,0;1.5708rad)
  baseObject = -> b_Z_axis_mount_platform_LM8_001_ [Edge759]
  diameter = 4
  invert = false
  matchOuter = false
  offset = 0
  thread = false
  type = 7
FEATURE [Part::FeaturePython] Nut020  label="M3-Nut017"  # Fasteners workbench fastener (typed FeaturePython)
  Placement = pos=(-264.588,20,29.9779) rot=(0,-1,0;1.5708rad)
  baseObject = -> b_Z_axis_mount_platform_LM8_001_ [Edge751]
  diameter = 4
  invert = true
  matchOuter = false
  offset = 0
  thread = false
  type = 7
FEATURE [Part::FeaturePython] Nut021  label="M3-Nut018"  # Fasteners workbench fastener (typed FeaturePython)
  Placement = pos=(-264.588,-20,29.9779) rot=(0,-1,0;1.5708rad)
  baseObject = -> b_Z_axis_mount_platform_LM8_001_ [Edge779]
  diameter = 4
  invert = true
  matchOuter = false
  offset = 0
  thread = false
  type = 7
FEATURE [Part::FeaturePython] Screw018  label="M3x10-Screw008"  # Fasteners workbench fastener (typed FeaturePython)
  Placement = pos=(-258.588,20,29.9779) rot=(0,1,0;1.5708rad)
  baseObject = -> b_Z_axis_mount_platform_LM8_001_ [Edge742]
  diameter = 4
  invert = false
  length = 3
  lengthCustom = 10
  matchOuter = false
  offset = 0
  thread = false
  type = 33
FEATURE [Part::FeaturePython] Screw019  label="M3x10-Screw009"  # Fasteners workbench fastener (typed FeaturePython)
  Placement = pos=(-258.588,-20,29.9779) rot=(0,1,0;1.5708rad)
  baseObject = -> b_Z_axis_mount_platform_LM8_001_ [Edge786]
  diameter = 4
  invert = false
  length = 3
  lengthCustom = 10
  matchOuter = false
  offset = 0
  thread = false
  type = 33
FEATURE [Part::FeaturePython] Screw020  label="M3x10-Screw010"  # Fasteners workbench fastener (typed FeaturePython)
  Placement = pos=(-197.412,20,29.9779) rot=(0,-1,0;1.5708rad)
  baseObject = -> b_Z_axis_mount_platform_LM8_001_ [Edge769]
  diameter = 4
  invert = true
  length = 3
  lengthCustom = 10
  matchOuter = false
  offset = 0
  thread = false
  type = 33
FEATURE [Part::FeaturePython] Screw021  label="M3x10-Screw011"  # Fasteners workbench fastener (typed FeaturePython)
  Placement = pos=(-197.412,-20,29.9779) rot=(0,-1,0;1.5708rad)
  baseObject = -> b_Z_axis_mount_platform_LM8_001_ [Edge796]
  diameter = 4
  invert = true
  length = 3
  lengthCustom = 10
  matchOuter = false
  offset = 0
  thread = false
  type = 33
FEATURE [Spreadsheet::Sheet] _PARTSLIST_  label="#PARTSLIST#"
  cells = A1=POS; B1=QTY; C1=IDENTNO; D1=DESCRIPTION; E1=SUPPLIER; F1=SUPP.IDENTNO; G1=SUPP.DESCRIPTION; H1=(FILENAME); A2=1; B2=1; C2=*; D2=*; E2=*; F2=*; G2=*; H2=Arm1_modified.FCStd; A3=2; B3=2; C3=*; D3=*; E3=*; F3=*; G3=*; H3=Ball_bearing_608.step; A4=3; B4=1; C4=*; D4=*; E4=*; F4=*; G4=*; H4=Ball_bearing_6806.step; A5=4; B5=1; C5=*; D5=*; E5=*; F5=*; G5=*; H5=Thrust_bearing_51107.step; A6=5; B6=1; C6=*; D6=*; E6=*; F6=*; G6=*; H6=Pulley_GT2-92t_j2.step; A7=6; B7=1; C7=*; D7=*; E7=*; F7=*; G7=*; H7=Pulley_GT2-23t_80t_arm1.step; A8=7; B8=1; C8=*; D8=*; E8=*; F8=*; G8=*; H8=Belt_GT2_300mm_23-92_arm1.step; A9=8; B9=1; C9=*; D9=*; E9=*; F9=*; G9=*; H9=Belt_GT2_400mm_20-80_arm1.step; A10=9; B10=1; C10=*; D10=*; E10=*; F10=*; G10=*; H10=Z-axis_mount_platform_LM8.FCStd; A11=10; B11=1; C11=*; D11=*; E11=*; F11=*; G11=*; H11=Stepper NEMA 17 -  20mm shaft.step; A12=11; B12=1; C12=*; D12=*; E12=*; F12=*; G12=*; H12=Pulley_GT2-20t.step; A13=12; B13=1; C13=*; D13=*; E13=*; F13=*; G13=*; H13=Nut_TR8_brass.step; A14=13; B14=4; C14=*; D14=*; E14=*; F14=*; G14=*; H14=Linear_bearing_lm8uu.step; A15=14; B15=1; C15=*; D15=*; E15=*; F15=*; G15=*; H15=Arm1_cover_modified.FCStd; A16=15; B16=1; C16=*; D16=*; E16=*; F16=*; G16=*; H16=Switch_endstop.step
FEATURE [Part::FeaturePython] Nut022  label="M5-Nut"  # Fasteners workbench fastener (typed FeaturePython)
  Placement = pos=(-174,25.5,16.5) rot=(0,-1,0;1.5708rad)
  baseObject = -> b_Z_axis_mount_platform_LM8_001_ [Edge6]
  diameter = 3
  invert = true
  matchOuter = false
  offset = 0
  thread = false
  type = 5
FEATURE [Part::FeaturePython] Nut023  label="M5-Nut001"  # Fasteners workbench fastener (typed FeaturePython)
  Placement = pos=(-174,25.5,34.5) rot=(0,-1,0;1.5708rad)
  baseObject = -> b_Z_axis_mount_platform_LM8_001_ [Edge29]
  diameter = 3
  invert = true
  matchOuter = false
  offset = 0
  thread = false
  type = 5
FEATURE [Part::FeaturePython] Nut024  label="M5-Nut002"  # Fasteners workbench fastener (typed FeaturePython)
  Placement = pos=(-174,-25.5,16.5) rot=(0,-1,0;1.5708rad)
  baseObject = -> b_Z_axis_mount_platform_LM8_001_ [Edge25]
  diameter = 3
  invert = true
  matchOuter = false
  offset = 0
  thread = false
  type = 5
FEATURE [Part::FeaturePython] Nut025  label="M5-Nut003"  # Fasteners workbench fastener (typed FeaturePython)
  Placement = pos=(-174,-25.5,34.5) rot=(0,-1,0;1.5708rad)
  baseObject = -> b_Z_axis_mount_platform_LM8_001_ [Edge27]
  diameter = 3
  invert = true
  matchOuter = false
  offset = 0
  thread = false
  type = 5
FEATURE [Part::FeaturePython] Washer001  label="M5-Washer"  # Fasteners workbench fastener (typed FeaturePython)
  Placement = pos=(-158,-25.5,16.5) rot=(0,1,0;1.5708rad)
  baseObject = -> b_Arm1_modified_001_ [Edge84]
  diameter = 6
  invert = true
  matchOuter = false
  offset = 0
  type = 3
FEATURE [Part::FeaturePython] Washer002  label="M5-Washer004"  # Fasteners workbench fastener (typed FeaturePython)
  Placement = pos=(-158,-25.5,34.5) rot=(0,1,0;1.5708rad)
  diameter = 6
  invert = true
  matchOuter = false
  offset = 0
  type = 3
FEATURE [Part::FeaturePython] Washer003  label="M5-Washer002"  # Fasteners workbench fastener (typed FeaturePython)
  Placement = pos=(-158,25.5,34.5) rot=(0,1,0;1.5708rad)
  baseObject = -> b_Arm1_modified_001_ [Edge89]
  diameter = 6
  invert = true
  matchOuter = false
  offset = 0
  type = 3
FEATURE [Part::FeaturePython] Washer004  label="M5-Washer003"  # Fasteners workbench fastener (typed FeaturePython)
  Placement = pos=(-158,25.5,16.5) rot=(0,1,0;1.5708rad)
  baseObject = -> b_Arm1_modified_001_ [Edge86]
  diameter = 6
  invert = true
  matchOuter = false
  offset = 0
  type = 3
FEATURE [Part::FeaturePython] Screw022  label="M5x25-Screw"  # Fasteners workbench fastener (typed FeaturePython)
  Placement = pos=(-156.9,-25.5,16.5) rot=(0,1,0;1.5708rad)
  baseObject = -> Washer001 [Edge1]
  diameter = 6
  invert = false
  length = 6
  lengthCustom = 25
  matchOuter = false
  offset = 0
  thread = false
  type = 33
FEATURE [Part::FeaturePython] Screw023  label="M5x25-Screw001"  # Fasteners workbench fastener (typed FeaturePython)
  Placement = pos=(-156.9,-25.5,34.5) rot=(0,1,0;1.5708rad)
  baseObject = -> Washer002 [Edge1]
  diameter = 6
  invert = false
  length = 6
  lengthCustom = 25
  matchOuter = false
  offset = 0
  thread = false
  type = 33
FEATURE [Part::FeaturePython] Screw024  label="M5x25-Screw002"  # Fasteners workbench fastener (typed FeaturePython)
  Placement = pos=(-156.9,25.5,16.5) rot=(0,1,0;1.5708rad)
  baseObject = -> Washer004 [Edge1]
  diameter = 6
  invert = false
  length = 6
  lengthCustom = 25
  matchOuter = false
  offset = 0
  thread = false
  type = 33
FEATURE [Part::FeaturePython] Screw025  label="M5x25-Screw003"  # Fasteners workbench fastener (typed FeaturePython)
  Placement = pos=(-156.9,25.5,34.5) rot=(0,1,0;1.5708rad)
  baseObject = -> Washer003 [Edge1]
  diameter = 6
  invert = false
  length = 6
  lengthCustom = 25
  matchOuter = false
  offset = 0
  thread = false
  type = 33
FEATURE [Spreadsheet::Sheet] Fasteners_BOM
  cells = A1=Type; B1=Qty; A2=DIN985 Nut M3; B2=6; A3=DIN985 Nut M4; B3=4; A4=DIN985 Nut M5; B4=4; A5=DIN985 Nut M8; B5=1; A6=ISO4017 Screw M8x45; B6=1; A7=ISO4032 Nut M3; B7=11; A8=ISO4762 Screw M3x10; B8=4; A9=ISO4762 Screw M5x25; B9=4; A10=ISO7045 Screw M3x10; B10=4; A11=ISO7045 Screw M3x12; B11=11; A12=ISO7045 Screw M3x20; B12=2; A13=ISO7089 Washer M5; B13=4; A14=ISO7089 Washer M8; B14=1
